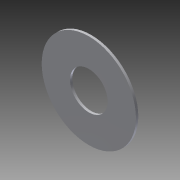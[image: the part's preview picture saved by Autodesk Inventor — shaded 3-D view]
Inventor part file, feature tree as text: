
AUTODESK INVENTOR PART (.ipt)
format: ipt  version: 2013 (Build 170138000, 138)  size: 77,824 bytes
history: native  units: mm
features: other x1, extrude x1, sketch x1
ambient origin geometry x8: Origin, YZ Plane, XZ Plane, XY Plane, X Axis, Y Axis, Z Axis, Center Point
feature tree (3):
  other  "ソリッド1"
  extrude  "押し出し1"  Depth=20.0mm
  sketch  "スケッチ1"
